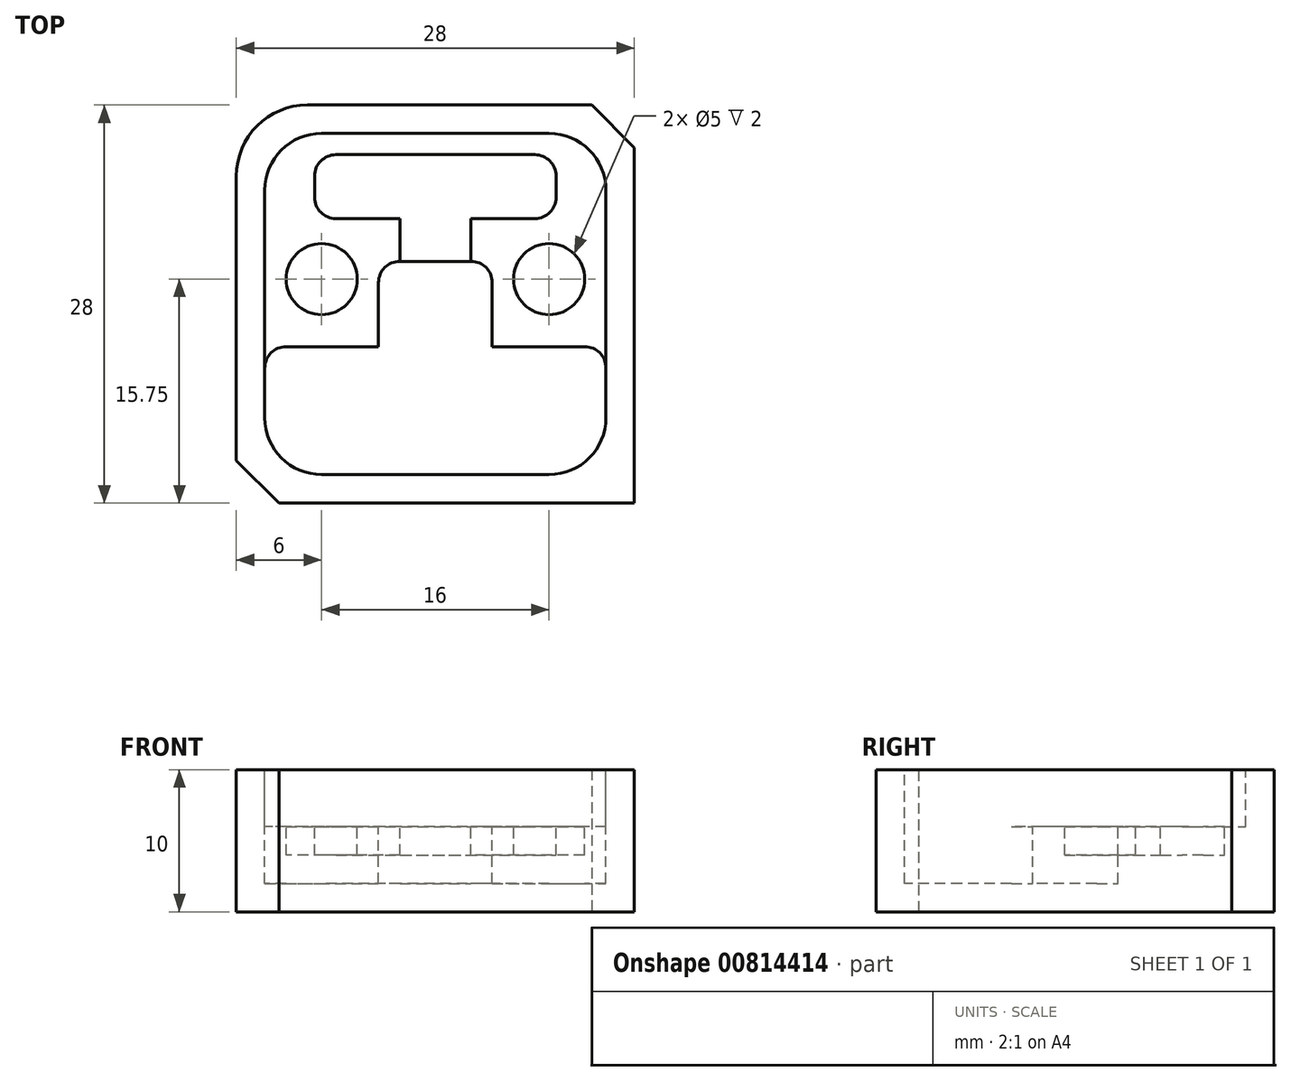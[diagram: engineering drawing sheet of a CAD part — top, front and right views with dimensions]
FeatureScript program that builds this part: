
annotation { "Feature Type Name" : "Feature", "Feature Type Description" : "" }
export const myFeature = defineFeature(function(context is Context, id is Id, definition is map)
    precondition{}
    {
        {
            var Q0;
            Q0=qCreatedBy(makeId("Top.planeOp"),FACE);
            var sketch = newSketch(context, id + "F0", { "sketchPlane" : qUnion([Q0])});
            skLineSegment(sketch, "E0.bottom", {"start": v(0, 0) * mm, "end": v(28, 0) * mm});
            skLineSegment(sketch, "E0.top", {"start": v(0, 28) * mm, "end": v(28, 28) * mm});
            skLineSegment(sketch, "E0.left", {"start": v(0, 0) * mm, "end": v(0, 28) * mm});
            skLineSegment(sketch, "E0.right", {"start": v(28, 0) * mm, "end": v(28, 28) * mm});
            skSolve(sketch);
        }
        {
            var Q0;
            Q0=makeQuery(id+"F0.imprint","IMPRINT",FACE,{"disambiguationData":[TD([[makeQuery(id+"F0.imprint","IMPRINT",EDGE,{"derivedFrom":sQuery(id+"F0.wireOp",EDGE,"E0.bottom")}),1.0]])]});
            extrude(context, id + "F1", {"entities" : qUnion([Q0]), "depth" : 10 * mm, "offsetDistance" : 25 * mm});
        }
        {
            var Q0;
            Q0=makeQuery(id+"F1.opExtrude","CAP_FACE",FACE,{"disambiguationData":[OSD([sQuery(id+"F0.wireOp",EDGE,"E0.bottom"),sQuery(id+"F0.wireOp",EDGE,"E0.top"),sQuery(id+"F0.wireOp",EDGE,"E0.left"),sQuery(id+"F0.wireOp",EDGE,"E0.right")])],"isStart":false});
            var sketch = newSketch(context, id + "F2", { "sketchPlane" : qUnion([Q0])});
            skLineSegment(sketch, "E1", {"start": v(0, 28) * mm, "end": v(28, 0) * mm, "construction": true});
            skPoint(sketch, "E2", {"position": v(14, 14) * mm});
            skLineSegment(sketch, "E3.bottom", {"start": v(22, 26) * mm, "end": v(6, 26) * mm});
            skLineSegment(sketch, "E3.top", {"start": v(22, 2) * mm, "end": v(6, 2) * mm});
            skLineSegment(sketch, "E3.left", {"start": v(26, 22) * mm, "end": v(26, 6) * mm});
            skLineSegment(sketch, "E3.right", {"start": v(2, 22) * mm, "end": v(2, 6) * mm});
            skPoint(sketch, "E4.visualSharp", {"position": v(2, 26) * mm});
            skArc(sketch, "E4.filletArc", {"start": v(6, 26) * mm, "mid": v(3.17, 24.83) * mm, "end": v(2, 22) * mm});
            skPoint(sketch, "E5.visualSharp", {"position": v(26, 26) * mm});
            skArc(sketch, "E5.filletArc", {"start": v(26, 22) * mm, "mid": v(24.83, 24.83) * mm, "end": v(22, 26) * mm});
            skPoint(sketch, "E6.visualSharp", {"position": v(26, 2) * mm});
            skArc(sketch, "E6.filletArc", {"start": v(22, 2) * mm, "mid": v(24.83, 3.17) * mm, "end": v(26, 6) * mm});
            skPoint(sketch, "E7.visualSharp", {"position": v(2, 2) * mm});
            skArc(sketch, "E7.filletArc", {"start": v(2, 6) * mm, "mid": v(3.17, 3.17) * mm, "end": v(6, 2) * mm});
            skSolve(sketch);
        }
        {
            var Q0;
            Q0=makeQuery(id+"F2.imprint","IMPRINT",FACE,{"disambiguationData":[TD([[makeQuery(id+"F2.imprint","IMPRINT",EDGE,{"derivedFrom":sQuery(id+"F2.wireOp",EDGE,"E3.bottom")}),1.0]])]});
            extrude(context, id + "F3", {"entities" : qUnion([Q0]), "operationType" : NewBodyOperationType.REMOVE, "oppositeDirection" : true, "depth" : 4 * mm, "offsetDistance" : 25 * mm});
        }
        {
            var Q0;
            Q0=makeQuery(id+"F3.boolean.opBoolean","COPY",FACE,{"derivedFrom":makeQuery(id+"F3.opExtrude","CAP_FACE",FACE,{"disambiguationData":[OSD([sQuery(id+"F2.wireOp",EDGE,"E3.bottom"),sQuery(id+"F2.wireOp",EDGE,"E3.top"),sQuery(id+"F2.wireOp",EDGE,"E3.left"),sQuery(id+"F2.wireOp",EDGE,"E3.right"),sQuery(id+"F2.wireOp",EDGE,"E4.filletArc"),sQuery(id+"F2.wireOp",EDGE,"E5.filletArc"),sQuery(id+"F2.wireOp",EDGE,"E6.filletArc"),sQuery(id+"F2.wireOp",EDGE,"E7.filletArc")])],"isStart":false})});
            var sketch = newSketch(context, id + "F4", { "sketchPlane" : qUnion([Q0])});
            skLineSegment(sketch, "E8", {"start": v(2, 14) * mm, "end": v(26, 14) * mm, "construction": true});
            skLineSegment(sketch, "E9", {"start": v(2, 11) * mm, "end": v(10, 11) * mm});
            skLineSegment(sketch, "E10", {"start": v(10, 11) * mm, "end": v(10, 17) * mm});
            skLineSegment(sketch, "E11", {"start": v(10, 17) * mm, "end": v(18, 17) * mm});
            skLineSegment(sketch, "E12", {"start": v(18, 17) * mm, "end": v(18, 11) * mm});
            skLineSegment(sketch, "E13", {"start": v(18, 11) * mm, "end": v(26, 11) * mm});
            skLineSegment(sketch, "E14", {"start": v(2, 11) * mm, "end": v(2, 6) * mm});
            skLineSegment(sketch, "E15", {"start": v(6, 2) * mm, "end": v(22, 2) * mm});
            skLineSegment(sketch, "E16", {"start": v(26, 6) * mm, "end": v(26, 11) * mm});
            skPoint(sketch, "E17.visualSharp", {"position": v(2, 2) * mm});
            skArc(sketch, "E17.filletArc", {"start": v(2, 6) * mm, "mid": v(3.17, 3.17) * mm, "end": v(6, 2) * mm});
            skPoint(sketch, "E18.visualSharp", {"position": v(26, 2) * mm});
            skArc(sketch, "E18.filletArc", {"start": v(22, 2) * mm, "mid": v(24.83, 3.17) * mm, "end": v(26, 6) * mm});
            skSolve(sketch);
        }
        {
            var Q0;
            Q0=makeQuery(id+"F4.imprint","IMPRINT",FACE,{"disambiguationData":[TD([[makeQuery(id+"F4.imprint","IMPRINT",EDGE,{"derivedFrom":sQuery(id+"F4.wireOp",EDGE,"E9")}),-1.0]])]});
            extrude(context, id + "F5", {"entities" : qUnion([Q0]), "operationType" : NewBodyOperationType.REMOVE, "oppositeDirection" : true, "depth" : 4 * mm, "offsetDistance" : 25 * mm});
        }
        {
            var Q0;
            Q0=makeQuery(id+"F1.opExtrude","SWEPT_EDGE",EDGE,{"disambiguationData":[OSD([sQuery(id+"F0.wireOp",EDGE,"E0.bottom"),sQuery(id+"F0.wireOp",EDGE,"E0.left")])]});
            var Q1;
            Q1=makeQuery(id+"F1.opExtrude","SWEPT_EDGE",EDGE,{"disambiguationData":[OSD([sQuery(id+"F0.wireOp",EDGE,"E0.top"),sQuery(id+"F0.wireOp",EDGE,"E0.right")])]});
            chamfer(context, id + "F6", {"entities" : qUnion([Q0, Q1]), "width" : 3 * mm, "tangentPropagation" : true});
        }
        {
            var Q0;
            Q0=makeQuery(id+"F5.boolean.opBoolean","COPY",EDGE,{"derivedFrom":makeQuery(id+"F5.opExtrude","SWEPT_EDGE",EDGE,{"disambiguationData":[OSD([sQuery(id+"F2.wireOp",EDGE,"E3.right"),sQuery(id+"F4.wireOp",EDGE,"E9"),sQuery(id+"F4.wireOp",EDGE,"E14")])]})});
            var Q1;
            Q1=makeQuery(id+"F5.boolean.opBoolean","COPY",EDGE,{"derivedFrom":makeQuery(id+"F5.opExtrude","SWEPT_EDGE",EDGE,{"disambiguationData":[OSD([sQuery(id+"F4.wireOp",EDGE,"E10"),sQuery(id+"F4.wireOp",EDGE,"E11")])]})});
            var Q2;
            Q2=makeQuery(id+"F5.boolean.opBoolean","COPY",EDGE,{"derivedFrom":makeQuery(id+"F5.opExtrude","SWEPT_EDGE",EDGE,{"disambiguationData":[OSD([sQuery(id+"F4.wireOp",EDGE,"E11"),sQuery(id+"F4.wireOp",EDGE,"E12")])]})});
            var Q3;
            Q3=makeQuery(id+"F5.boolean.opBoolean","COPY",EDGE,{"derivedFrom":makeQuery(id+"F5.opExtrude","SWEPT_EDGE",EDGE,{"disambiguationData":[OSD([sQuery(id+"F2.wireOp",EDGE,"E3.left"),sQuery(id+"F4.wireOp",EDGE,"E13"),sQuery(id+"F4.wireOp",EDGE,"E16")])]})});
            fillet(context, id + "F7", {"entities" : qUnion([Q0, Q1, Q2, Q3]), "radius" : 1.5 * mm, "tangentPropagation" : true, "allowEdgeOverflow" : false});
        }
        {
            var Q0;
            Q0=makeQuery(id+"F1.opExtrude","SWEPT_EDGE",EDGE,{"disambiguationData":[OSD([sQuery(id+"F0.wireOp",EDGE,"E0.top"),sQuery(id+"F0.wireOp",EDGE,"E0.left")])]});
            fillet(context, id + "F8", {"entities" : qUnion([Q0]), "radius" : 5 * mm, "tangentPropagation" : true, "allowEdgeOverflow" : false});
        }
        {
            var Q0;
            Q0=makeQuery(id+"F3.boolean.opBoolean","COPY",FACE,{"derivedFrom":makeQuery(id+"F3.opExtrude","CAP_FACE",FACE,{"disambiguationData":[OSD([sQuery(id+"F2.wireOp",EDGE,"E3.bottom"),sQuery(id+"F2.wireOp",EDGE,"E3.top"),sQuery(id+"F2.wireOp",EDGE,"E3.left"),sQuery(id+"F2.wireOp",EDGE,"E3.right"),sQuery(id+"F2.wireOp",EDGE,"E4.filletArc"),sQuery(id+"F2.wireOp",EDGE,"E5.filletArc"),sQuery(id+"F2.wireOp",EDGE,"E6.filletArc"),sQuery(id+"F2.wireOp",EDGE,"E7.filletArc")])],"isStart":false})});
            var sketch = newSketch(context, id + "F9", { "sketchPlane" : qUnion([Q0])});
            skPoint(sketch, "E19.endSnap0", {"position": v(18, 13.25) * mm});
            skLineSegment(sketch, "E20", {"start": v(26, 15.75) * mm, "end": v(2, 15.75) * mm, "construction": true});
            skCircle(sketch, "E21", {"center": v(6, 15.75) * mm, "radius": 2.5 * mm});
            skCircle(sketch, "E22", {"center": v(22, 15.75) * mm, "radius": 2.5 * mm});
            skLineSegment(sketch, "E23", {"start": v(14, 17) * mm, "end": v(14, 24) * mm, "construction": true});
            skLineSegment(sketch, "E24", {"start": v(11.5, 17) * mm, "end": v(11.5, 20) * mm});
            skLineSegment(sketch, "E25", {"start": v(11.5, 20) * mm, "end": v(7, 20) * mm});
            skLineSegment(sketch, "E26", {"start": v(5.5, 21.5) * mm, "end": v(5.5, 23) * mm});
            skLineSegment(sketch, "E27", {"start": v(7, 24.5) * mm, "end": v(21, 24.5) * mm});
            skLineSegment(sketch, "E28", {"start": v(22.5, 23) * mm, "end": v(22.5, 21.5) * mm});
            skLineSegment(sketch, "E29", {"start": v(21, 20) * mm, "end": v(16.5, 20) * mm});
            skLineSegment(sketch, "E30", {"start": v(16.5, 20) * mm, "end": v(16.5, 17) * mm});
            skLineSegment(sketch, "E31", {"start": v(16.5, 17) * mm, "end": v(11.5, 17) * mm});
            skPoint(sketch, "E32.visualSharp", {"position": v(5.5, 24.5) * mm});
            skArc(sketch, "E32.filletArc", {"start": v(7, 24.5) * mm, "mid": v(5.94, 24.06) * mm, "end": v(5.5, 23) * mm});
            skPoint(sketch, "E33.visualSharp", {"position": v(5.5, 20) * mm});
            skArc(sketch, "E33.filletArc", {"start": v(5.5, 21.5) * mm, "mid": v(5.94, 20.44) * mm, "end": v(7, 20) * mm});
            skPoint(sketch, "E34.visualSharp", {"position": v(22.5, 24.5) * mm});
            skArc(sketch, "E34.filletArc", {"start": v(22.5, 23) * mm, "mid": v(22.06, 24.06) * mm, "end": v(21, 24.5) * mm});
            skPoint(sketch, "E35.visualSharp", {"position": v(22.5, 20) * mm});
            skArc(sketch, "E35.filletArc", {"start": v(21, 20) * mm, "mid": v(22.06, 20.44) * mm, "end": v(22.5, 21.5) * mm});
            skSolve(sketch);
        }
        {
            var Q0;
            Q0=makeQuery(id+"F9.imprint","IMPRINT",FACE,{"disambiguationData":[TD([[makeQuery(id+"F9.imprint","IMPRINT",EDGE,{"derivedFrom":sQuery(id+"F9.wireOp",EDGE,"E24")}),-1.0]])]});
            var Q1;
            Q1=makeQuery(id+"F9.imprint","IMPRINT",FACE,{"disambiguationData":[TD([[makeQuery(id+"F9.imprint","IMPRINT",EDGE,{"derivedFrom":sQuery(id+"F9.wireOp",EDGE,"E22")}),1.0]])]});
            var Q2;
            Q2=makeQuery(id+"F9.imprint","IMPRINT",FACE,{"disambiguationData":[TD([[makeQuery(id+"F9.imprint","IMPRINT",EDGE,{"derivedFrom":sQuery(id+"F9.wireOp",EDGE,"E21")}),1.0]])]});
            extrude(context, id + "F10", {"entities" : qUnion([Q0, Q1, Q2]), "operationType" : NewBodyOperationType.REMOVE, "oppositeDirection" : true, "depth" : 2 * mm, "offsetDistance" : 25 * mm});
        }
    });
